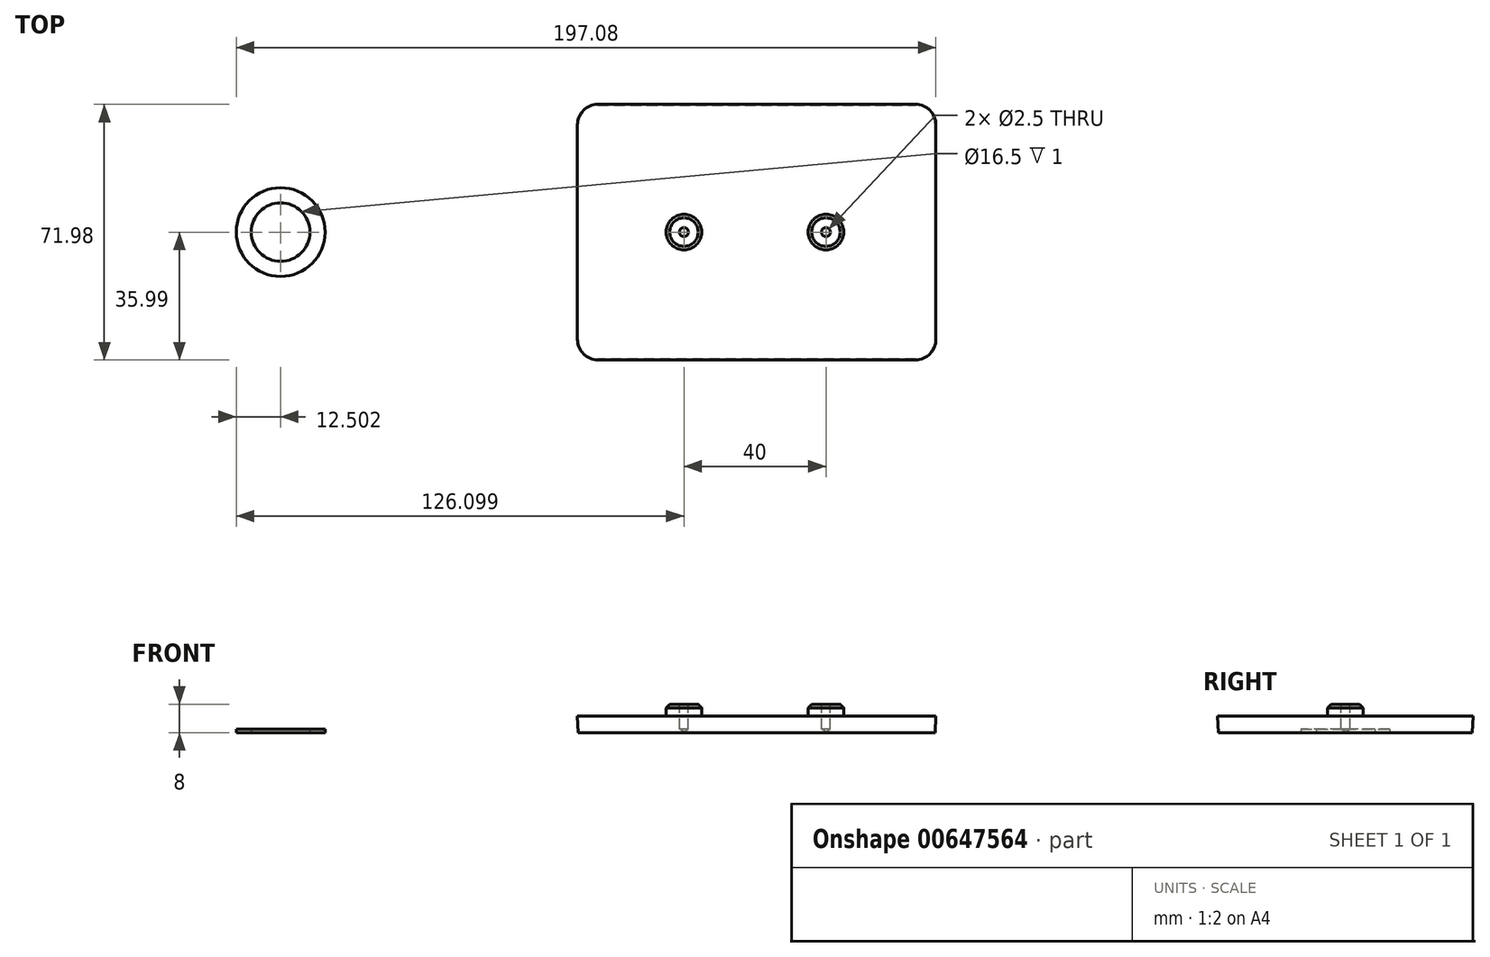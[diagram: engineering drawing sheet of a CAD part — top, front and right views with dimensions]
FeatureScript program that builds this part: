
annotation { "Feature Type Name" : "Feature", "Feature Type Description" : "" }
export const myFeature = defineFeature(function(context is Context, id is Id, definition is map)
    precondition{}
    {
        {
            var Q0;
            Q0=qCreatedBy(makeId("Top.planeOp"),FACE);
            var sketch = newSketch(context, id + "F0", { "sketchPlane" : qUnion([Q0])});
            skLineSegment(sketch, "E0.bottom", {"start": v(44.75, -35.75) * mm, "end": v(-44.75, -35.75) * mm});
            skLineSegment(sketch, "E0.top", {"start": v(44.75, 35.75) * mm, "end": v(-44.75, 35.75) * mm});
            skLineSegment(sketch, "E0.left", {"start": v(50.25, -30.25) * mm, "end": v(50.25, 30.25) * mm});
            skLineSegment(sketch, "E0.right", {"start": v(-50.25, -30.25) * mm, "end": v(-50.25, 30.25) * mm});
            skPoint(sketch, "E0.middle", {"position": v(0, 0) * mm});
            skPoint(sketch, "E1.visualSharp", {"position": v(-50.25, 35.75) * mm});
            skArc(sketch, "E1.filletArc", {"start": v(-44.75, 35.75) * mm, "mid": v(-48.64, 34.14) * mm, "end": v(-50.25, 30.25) * mm});
            skPoint(sketch, "E2.visualSharp", {"position": v(50.25, 35.75) * mm});
            skArc(sketch, "E2.filletArc", {"start": v(50.25, 30.25) * mm, "mid": v(48.64, 34.14) * mm, "end": v(44.75, 35.75) * mm});
            skPoint(sketch, "E3.visualSharp", {"position": v(50.25, -35.75) * mm});
            skArc(sketch, "E3.filletArc", {"start": v(44.75, -35.75) * mm, "mid": v(48.64, -34.14) * mm, "end": v(50.25, -30.25) * mm});
            skPoint(sketch, "E4.visualSharp", {"position": v(-50.25, -35.75) * mm});
            skArc(sketch, "E4.filletArc", {"start": v(-50.25, -30.25) * mm, "mid": v(-48.64, -34.14) * mm, "end": v(-44.75, -35.75) * mm});
            skSolve(sketch);
        }
        {
            var Q0;
            Q0 = qSketchRegion(id + "F0", true);
            extrude(context, id + "F1", {"entities" : qUnion([Q0]), "depth" : 4.6 * mm, "offsetDistance" : 25 * mm, "hasDraft" : true, "draftAngle" : 3 * degree});
        }
        {
            var Q0;
            Q0=makeQuery(id+"F1.opExtrude","CAP_FACE",FACE,{"disambiguationData":[OSD([sQuery(id+"F0.wireOp",EDGE,"E0.bottom"),sQuery(id+"F0.wireOp",EDGE,"E0.top"),sQuery(id+"F0.wireOp",EDGE,"E0.left"),sQuery(id+"F0.wireOp",EDGE,"E0.right"),sQuery(id+"F0.wireOp",EDGE,"E1.filletArc"),sQuery(id+"F0.wireOp",EDGE,"E2.filletArc"),sQuery(id+"F0.wireOp",EDGE,"E3.filletArc"),sQuery(id+"F0.wireOp",EDGE,"E4.filletArc")])],"isStart":false});
            var sketch = newSketch(context, id + "F2", { "sketchPlane" : qUnion([Q0])});
            skLineSegment(sketch, "E5", {"start": v(-50.5, 0) * mm, "end": v(50.5, 0) * mm, "construction": true});
            skLineSegment(sketch, "E6", {"start": v(0, 36) * mm, "end": v(0, -36) * mm, "construction": true});
            skCircle(sketch, "E7", {"center": v(-20.5, 0) * mm, "radius": 5 * mm});
            skCircle(sketch, "E8", {"center": v(19.5, 0) * mm, "radius": 5 * mm});
            skSolve(sketch);
        }
        {
            var Q0;
            Q0=makeQuery(id+"F2.imprint","IMPRINT",FACE,{"disambiguationData":[TD([[makeQuery(id+"F2.imprint","IMPRINT",EDGE,{"derivedFrom":sQuery(id+"F2.wireOp",EDGE,"E8")}),1.0]])]});
            var Q1;
            Q1=makeQuery(id+"F2.imprint","IMPRINT",FACE,{"disambiguationData":[TD([[makeQuery(id+"F2.imprint","IMPRINT",EDGE,{"derivedFrom":sQuery(id+"F2.wireOp",EDGE,"E7")}),1.0]])]});
            extrude(context, id + "F3", {"entities" : qUnion([Q0, Q1]), "operationType" : NewBodyOperationType.ADD, "depth" : 3.4 * mm, "offsetDistance" : 25 * mm});
        }
        {
            var Q0;
            Q0=makeQuery(id+"F3.opExtrude","CAP_EDGE",EDGE,{"disambiguationData":[OSD([sQuery(id+"F2.wireOp",EDGE,"E7")])],"isStart":false});
            var Q1;
            Q1=makeQuery(id+"F3.opExtrude","CAP_EDGE",EDGE,{"disambiguationData":[OSD([sQuery(id+"F2.wireOp",EDGE,"E8")])],"isStart":false});
            chamfer(context, id + "F4", {"entities" : qUnion([Q0, Q1]), "width" : 1 * mm, "tangentPropagation" : true});
        }
        {
            var Q0;
            Q0=makeQuery(id+"F3.opExtrude","CAP_FACE",FACE,{"disambiguationData":[OSD([sQuery(id+"F2.wireOp",EDGE,"E7")])],"isStart":false});
            var sketch = newSketch(context, id + "F5", { "sketchPlane" : qUnion([Q0])});
            skPoint(sketch, "E9", {"position": v(-20.5, 0) * mm});
            skCircle(sketch, "E10.0", {"center": v(19.5, 0) * mm, "radius": 4 * mm, "construction": true});
            skCircle(sketch, "E11.0", {"center": v(-20.5, 0) * mm, "radius": 4 * mm, "construction": true});
            skSolve(sketch);
        }
        {
            var Q0;
            Q0=sQuery(id+"F5.wireOp",VERTEX,"E9");
            var Q1;
            Q1=sQuery(id+"F5.wireOp",VERTEX,"E10.0.center");
            var Q2;
            Q2=makeQuery(id+"F1.opExtrude","SWEPT_BODY",BODY,{"disambiguationData":[OSD([sQuery(id+"F0.wireOp",EDGE,"E0.bottom"),sQuery(id+"F0.wireOp",EDGE,"E0.top"),sQuery(id+"F0.wireOp",EDGE,"E0.left"),sQuery(id+"F0.wireOp",EDGE,"E0.right"),sQuery(id+"F0.wireOp",EDGE,"E1.filletArc"),sQuery(id+"F0.wireOp",EDGE,"E2.filletArc"),sQuery(id+"F0.wireOp",EDGE,"E3.filletArc"),sQuery(id+"F0.wireOp",EDGE,"E4.filletArc")])]});
            hole(context, id + "F6", {"style" : HoleStyle.SIMPLE, "endStyle" : HoleEndStyle.BLIND, "holeDiameter" : 2.5 * mm, "majorDiameter" : 5 * mm, "holeDepth" : 7 * mm, "isTappedThrough" : true, "tappedDepth" : 12 * mm, "tapClearance" : 3, "startFromSketch" : true, "locations" : qUnion([Q0, Q1]), "scope" : qUnion([Q2])});
        }
        {
            var Q0;
            Q0=qCreatedBy(makeId("Top.planeOp"),FACE);
            var sketch = newSketch(context, id + "F7", { "sketchPlane" : qUnion([Q0])});
            skCircle(sketch, "E12", {"center": v(-134.09, 0) * mm, "radius": 12.5 * mm});
            skCircle(sketch, "E13", {"center": v(-134.09, 0) * mm, "radius": 8.25 * mm});
            skSolve(sketch);
        }
        {
            var Q0;
            Q0=makeQuery(id+"F7.imprint","IMPRINT",FACE,{"disambiguationData":[TD([[makeQuery(id+"F7.imprint","IMPRINT",EDGE,{"derivedFrom":sQuery(id+"F7.wireOp",EDGE,"E12")}),1.0]])]});
            extrude(context, id + "F8", {"entities" : qUnion([Q0]), "depth" : 1 * mm, "offsetDistance" : 25 * mm});
        }
    });
